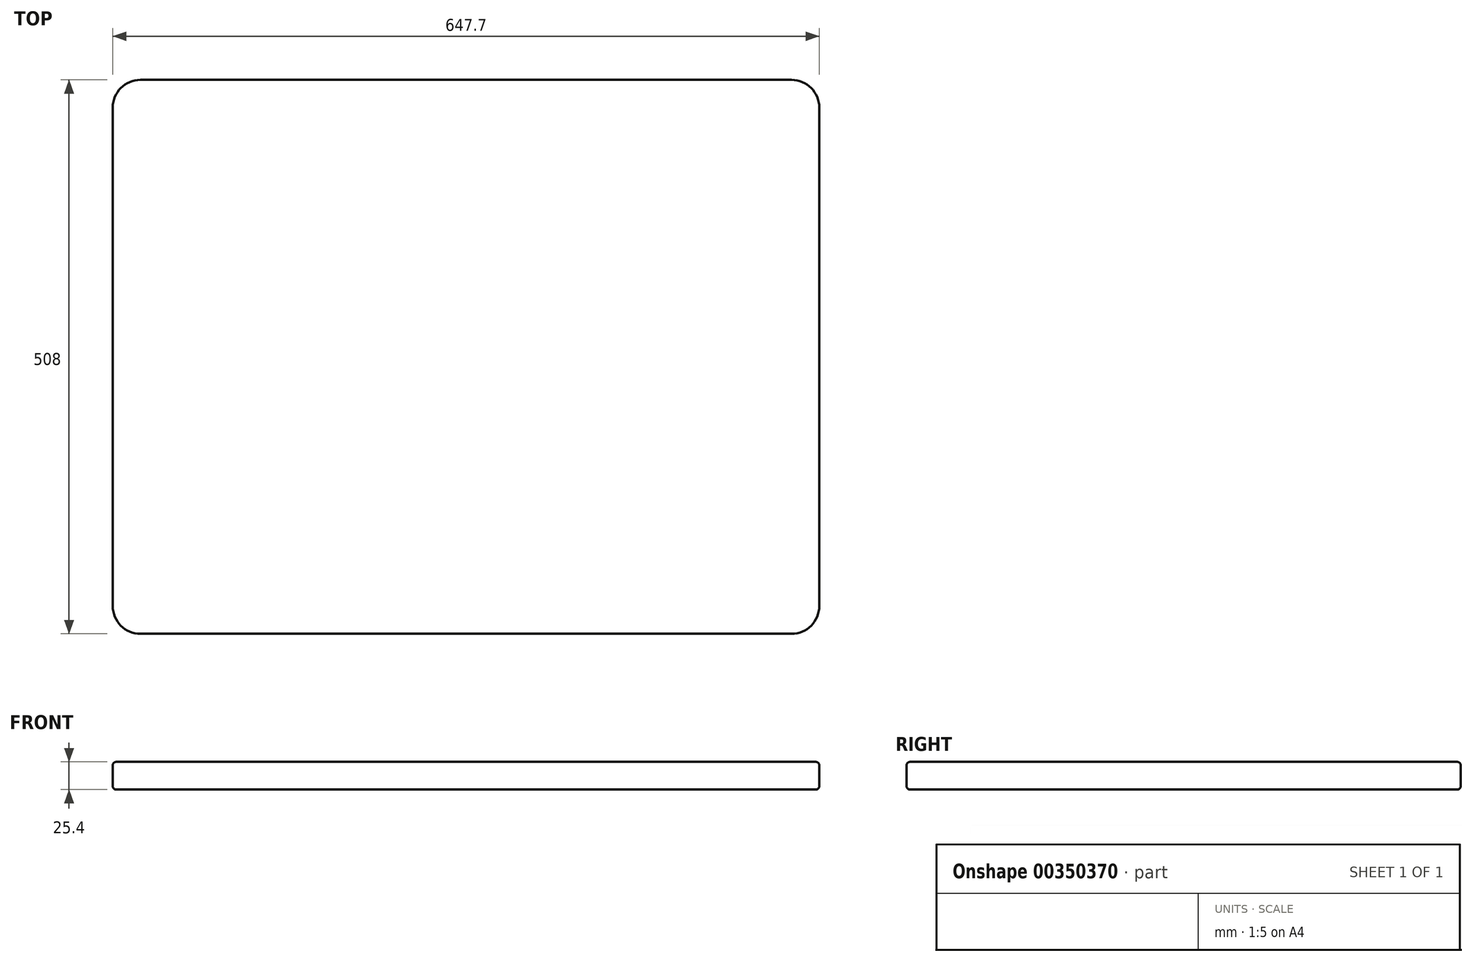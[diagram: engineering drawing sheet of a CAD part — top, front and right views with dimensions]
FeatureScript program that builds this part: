
annotation { "Feature Type Name" : "Feature", "Feature Type Description" : "" }
export const myFeature = defineFeature(function(context is Context, id is Id, definition is map)
    precondition{}
    {
        {
            var Q0;
            Q0=qCreatedBy(makeId("Top.planeOp"),FACE);
            var sketch = newSketch(context, id + "F0", { "sketchPlane" : qUnion([Q0])});
            skLineSegment(sketch, "E0.bottom", {"start": v(298.45, 254) * mm, "end": v(-298.45, 254) * mm});
            skLineSegment(sketch, "E0.top", {"start": v(298.45, -254) * mm, "end": v(-298.45, -254) * mm});
            skLineSegment(sketch, "E0.left", {"start": v(323.85, 228.6) * mm, "end": v(323.85, -228.6) * mm});
            skLineSegment(sketch, "E0.right", {"start": v(-323.85, 228.6) * mm, "end": v(-323.85, -228.6) * mm});
            skPoint(sketch, "E0.middle", {"position": v(0, 0) * mm});
            skPoint(sketch, "E1.visualSharp", {"position": v(-323.85, -254) * mm});
            skArc(sketch, "E1.filletArc", {"start": v(-323.85, -228.6) * mm, "mid": v(-316.41, -246.56) * mm, "end": v(-298.45, -254) * mm});
            skPoint(sketch, "E2.visualSharp", {"position": v(-323.85, 254) * mm});
            skArc(sketch, "E2.filletArc", {"start": v(-298.45, 254) * mm, "mid": v(-316.41, 246.56) * mm, "end": v(-323.85, 228.6) * mm});
            skPoint(sketch, "E3.visualSharp", {"position": v(323.85, 254) * mm});
            skArc(sketch, "E3.filletArc", {"start": v(323.85, 228.6) * mm, "mid": v(316.41, 246.56) * mm, "end": v(298.45, 254) * mm});
            skPoint(sketch, "E4.visualSharp", {"position": v(323.85, -254) * mm});
            skArc(sketch, "E4.filletArc", {"start": v(298.45, -254) * mm, "mid": v(316.41, -246.56) * mm, "end": v(323.85, -228.6) * mm});
            skSolve(sketch);
        }
        {
            var Q0;
            Q0=makeQuery(id+"F0.imprint","IMPRINT",FACE,{"disambiguationData":[TD([[makeQuery(id+"F0.imprint","IMPRINT",EDGE,{"derivedFrom":sQuery(id+"F0.wireOp",EDGE,"E0.bottom")}),1.0]])]});
            extrude(context, id + "F1", {"entities" : qUnion([Q0]), "endBound" : BoundingType.SYMMETRIC, "depth" : 25.4 * mm});
        }
        {
            var Q0;
            Q0=makeQuery(id+"F1.opExtrude","CAP_EDGE",EDGE,{"disambiguationData":[OSD([sQuery(id+"F0.wireOp",EDGE,"E0.top")])],"isStart":false});
            var Q1;
            Q1=makeQuery(id+"F1.opExtrude","CAP_EDGE",EDGE,{"disambiguationData":[OSD([sQuery(id+"F0.wireOp",EDGE,"E0.bottom")])],"isStart":true});
            fillet(context, id + "F2", {"entities" : qUnion([Q0, Q1]), "radius" : 3.17 * mm, "tangentPropagation" : true, "allowEdgeOverflow" : false});
        }
    });
